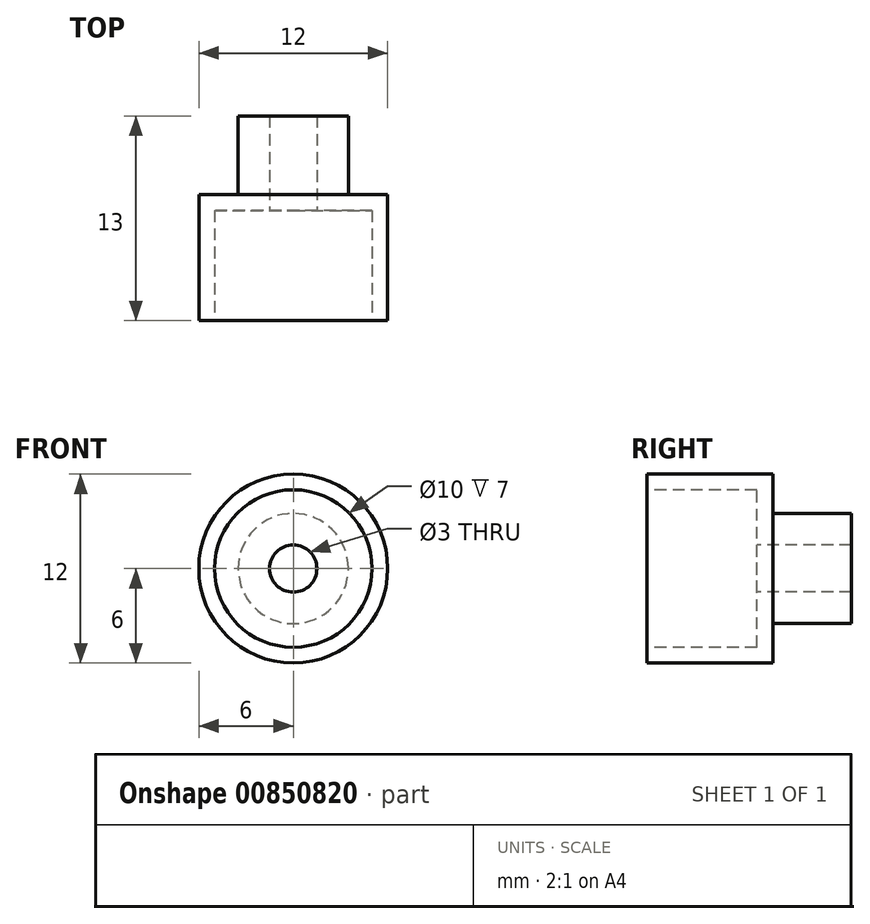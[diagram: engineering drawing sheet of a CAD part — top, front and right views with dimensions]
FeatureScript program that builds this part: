
annotation { "Feature Type Name" : "Feature", "Feature Type Description" : "" }
export const myFeature = defineFeature(function(context is Context, id is Id, definition is map)
    precondition{}
    {
        {
            var Q0;
            Q0=qCreatedBy(makeId("Front.planeOp"),FACE);
            var sketch = newSketch(context, id + "F0", { "sketchPlane" : qUnion([Q0])});
            skCircle(sketch, "E0", {"center": v(0, 0) * mm, "radius": 5 * mm});
            skCircle(sketch, "E1", {"center": v(0, 0) * mm, "radius": 6 * mm});
            skSolve(sketch);
        }
        {
            var Q0;
            Q0=makeQuery(id+"F0.imprint","IMPRINT",FACE,{"disambiguationData":[TD([[makeQuery(id+"F0.imprint","IMPRINT",EDGE,{"derivedFrom":sQuery(id+"F0.wireOp",EDGE,"E0")}),1.0]])]});
            var Q1;
            Q1=makeQuery(id+"F0.imprint","IMPRINT",FACE,{"disambiguationData":[TD([[makeQuery(id+"F0.imprint","IMPRINT",EDGE,{"derivedFrom":sQuery(id+"F0.wireOp",EDGE,"E0")}),-1.0]])]});
            extrude(context, id + "F1", {"entities" : qUnion([Q0, Q1]), "oppositeDirection" : true, "depth" : 8 * mm, "offsetDistance" : 25 * mm});
        }
        {
            var Q0;
            Q0=qCreatedBy(makeId("Front.planeOp"),FACE);
            cPlane(context, id + "F2", {"entities" : qUnion([Q0]), "cplaneType" : CPlaneType.OFFSET, "offset" : 8 * mm, "oppositeDirection" : true, "width" : 150 * mm, "height" : 150 * mm});
        }
        {
            var Q0;
            Q0=qCreatedBy(id+"F2.planeOp",FACE);
            var sketch = newSketch(context, id + "F3", { "sketchPlane" : qUnion([Q0])});
            skCircle(sketch, "E2", {"center": v(0, 0) * mm, "radius": 3.5 * mm});
            skCircle(sketch, "E3", {"center": v(0, 0) * mm, "radius": 1.5 * mm});
            skSolve(sketch);
        }
        {
            var Q0;
            Q0=makeQuery(id+"F3.imprint","IMPRINT",FACE,{"disambiguationData":[TD([[makeQuery(id+"F3.imprint","IMPRINT",EDGE,{"derivedFrom":sQuery(id+"F3.wireOp",EDGE,"E2")}),1.0]])]});
            var Q1;
            Q1=makeQuery(id+"F3.imprint","IMPRINT",FACE,{"disambiguationData":[TD([[makeQuery(id+"F3.imprint","IMPRINT",EDGE,{"derivedFrom":sQuery(id+"F3.wireOp",EDGE,"E3")}),1.0]])]});
            extrude(context, id + "F4", {"entities" : qUnion([Q0, Q1]), "operationType" : NewBodyOperationType.ADD, "oppositeDirection" : true, "depth" : 5 * mm, "offsetDistance" : 25 * mm});
        }
        {
            var Q0;
            Q0=qCreatedBy(makeId("Front.planeOp"),FACE);
            var sketch = newSketch(context, id + "F5", { "sketchPlane" : qUnion([Q0])});
            skCircle(sketch, "E4", {"center": v(0, 0) * mm, "radius": 5 * mm});
            skSolve(sketch);
        }
        {
            var Q0;
            Q0=qSketchRegion(id+"F5",true);
            extrude(context, id + "F6", {"entities" : qUnion([Q0]), "operationType" : NewBodyOperationType.REMOVE, "oppositeDirection" : true, "depth" : 7 * mm, "offsetDistance" : 25 * mm});
        }
        {
            var Q0;
            Q0=qCreatedBy(makeId("Front.planeOp"),FACE);
            var sketch = newSketch(context, id + "F7", { "sketchPlane" : qUnion([Q0])});
            skCircle(sketch, "E5", {"center": v(0, 0) * mm, "radius": 1.5 * mm});
            skSolve(sketch);
        }
        {
            var Q0;
            Q0=qSketchRegion(id+"F7",true);
            extrude(context, id + "F8", {"entities" : qUnion([Q0]), "operationType" : NewBodyOperationType.REMOVE, "oppositeDirection" : true, "depth" : 25 * mm, "offsetDistance" : 25 * mm});
        }
    });
